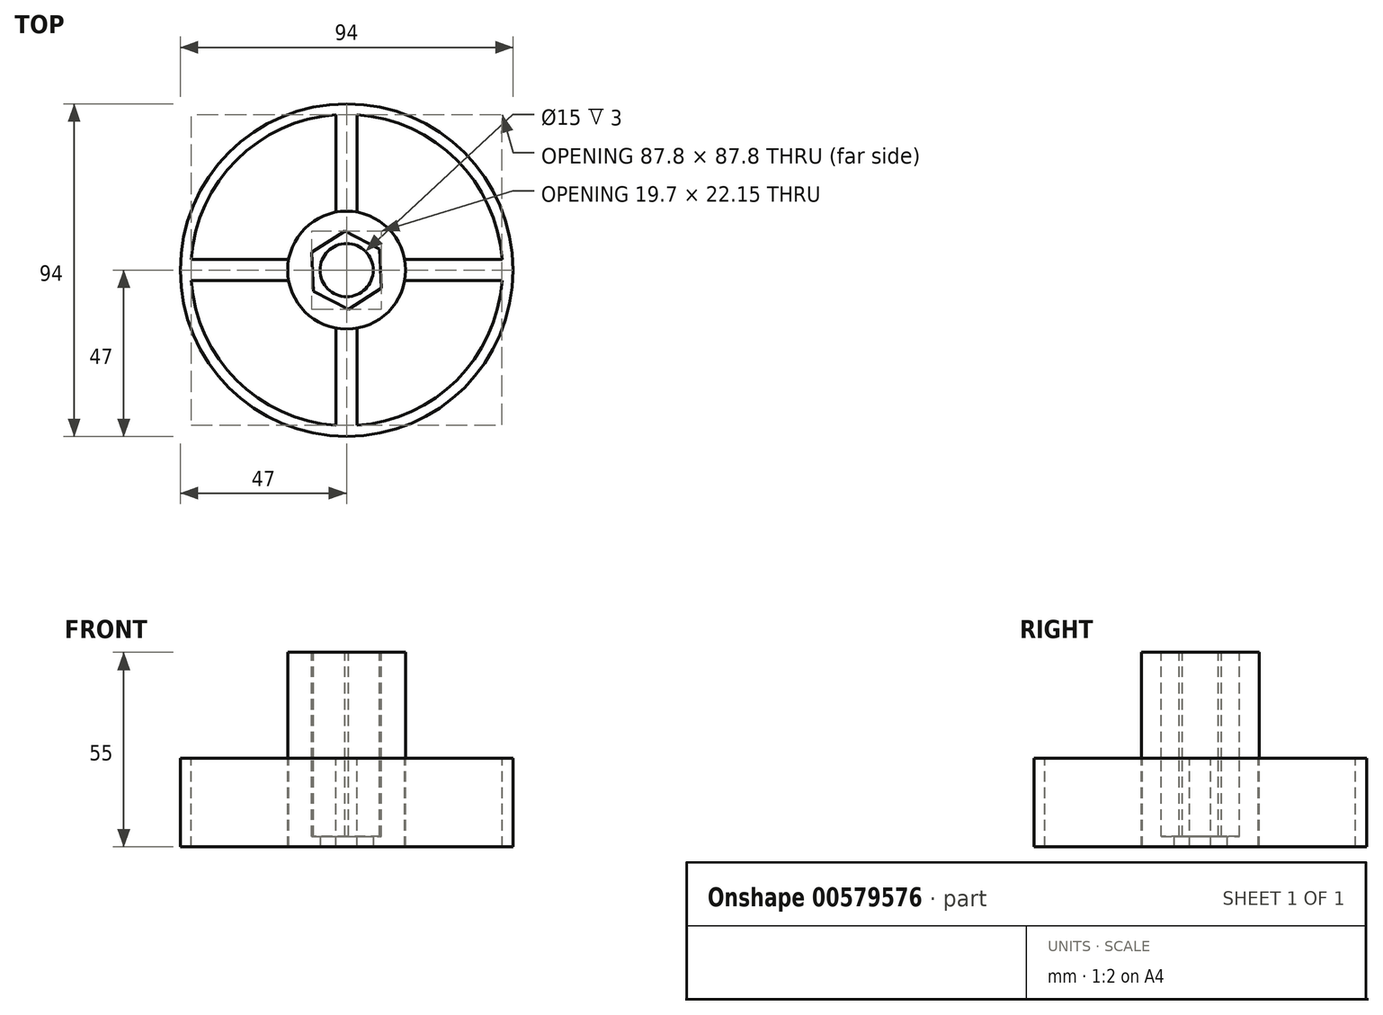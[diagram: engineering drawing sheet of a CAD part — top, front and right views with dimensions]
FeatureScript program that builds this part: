
annotation { "Feature Type Name" : "Feature", "Feature Type Description" : "" }
export const myFeature = defineFeature(function(context is Context, id is Id, definition is map)
    precondition{}
    {
        {
            var Q0;
            Q0=qCreatedBy(makeId("Top.planeOp"),FACE);
            var sketch = newSketch(context, id + "F0", { "sketchPlane" : qUnion([Q0])});
            skCircle(sketch, "E0.cCircle", {"center": v(0, 0) * mm, "radius": 9.6 * mm, "construction": true});
            skLineSegment(sketch, "E0.0", {"start": v(-9.85, 5.08) * mm, "end": v(-0.52, 11.07) * mm});
            skLineSegment(sketch, "E0.1", {"start": v(-0.52, 11.07) * mm, "end": v(9.33, 6) * mm});
            skLineSegment(sketch, "E0.2", {"start": v(9.33, 6) * mm, "end": v(9.85, -5.08) * mm});
            skLineSegment(sketch, "E0.3", {"start": v(9.85, -5.08) * mm, "end": v(0.52, -11.07) * mm});
            skLineSegment(sketch, "E0.4", {"start": v(0.52, -11.07) * mm, "end": v(-9.33, -6) * mm});
            skLineSegment(sketch, "E0.5", {"start": v(-9.33, -6) * mm, "end": v(-9.85, 5.08) * mm});
            skPoint(sketch, "E0.0.midPoint", {"position": v(-5.19, 8.08) * mm});
            skSolve(sketch);
        }
        {
            var Q0;
            Q0=qCreatedBy(makeId("Top.planeOp"),FACE);
            var sketch = newSketch(context, id + "F1", { "sketchPlane" : qUnion([Q0])});
            skCircle(sketch, "E1", {"center": v(0, 0) * mm, "radius": 16.65 * mm});
            skSolve(sketch);
        }
        {
            var Q0;
            Q0=makeQuery(id+"F1.imprint","IMPRINT",FACE,{"disambiguationData":[TD([[makeQuery(id+"F1.imprint","IMPRINT",EDGE,{"derivedFrom":sQuery(id+"F1.wireOp",EDGE,"E1")}),1.0]])]});
            extrude(context, id + "F2", {"entities" : qUnion([Q0]), "oppositeDirection" : true, "depth" : 30 * mm, "offsetDistance" : 25 * mm});
        }
        {
            var Q0;
            Q0=makeQuery(id+"F0.imprint","IMPRINT",FACE,{"disambiguationData":[TD([[makeQuery(id+"F0.imprint","IMPRINT",EDGE,{"derivedFrom":sQuery(id+"F0.wireOp",EDGE,"E0.0")}),-1.0]])]});
            extrude(context, id + "F3", {"entities" : qUnion([Q0]), "operationType" : NewBodyOperationType.REMOVE, "oppositeDirection" : true, "depth" : 31 * mm, "offsetDistance" : 25 * mm});
        }
        {
            var Q0;
            Q0=makeQuery(id+"F2.opExtrude","CAP_FACE",FACE,{"disambiguationData":[OSD([sQuery(id+"F1.wireOp",EDGE,"E1")])],"isStart":false});
            var sketch = newSketch(context, id + "F4", { "sketchPlane" : qUnion([Q0])});
            skCircle(sketch, "E2", {"center": v(0, 0) * mm, "radius": 7.5 * mm});
            skSolve(sketch);
        }
        {
            var Q0;
            Q0=makeQuery(id+"F4.imprint","IMPRINT",FACE,{"disambiguationData":[TD([[makeQuery(id+"F4.imprint","IMPRINT",EDGE,{"derivedFrom":sQuery(id+"F4.wireOp",EDGE,"E2")}),1.0]])]});
            extrude(context, id + "F5", {"entities" : qUnion([Q0]), "operationType" : NewBodyOperationType.REMOVE, "oppositeDirection" : true, "depth" : 25 * mm});
        }
        {
            var Q0;
            Q0=makeQuery(id+"F2.opExtrude","CAP_FACE",FACE,{"disambiguationData":[OSD([sQuery(id+"F1.wireOp",EDGE,"E1")])],"isStart":false});
            var sketch = newSketch(context, id + "F6", { "sketchPlane" : qUnion([Q0])});
            skCircle(sketch, "E3", {"center": v(0, 0) * mm, "radius": 47 * mm});
            skCircle(sketch, "E4", {"center": v(0, 0) * mm, "radius": 44 * mm});
            skPoint(sketch, "E5", {"position": v(-3, 0) * mm});
            skPoint(sketch, "E6", {"position": v(3, 0) * mm});
            skPoint(sketch, "E7", {"position": v(0, 3) * mm});
            skPoint(sketch, "E8", {"position": v(0, -3) * mm});
            skLineSegment(sketch, "E9", {"start": v(-3, 0) * mm, "end": v(-3, 43.9) * mm});
            skLineSegment(sketch, "E10", {"start": v(3, 0) * mm, "end": v(3, 43.9) * mm});
            skLineSegment(sketch, "E11", {"start": v(-3, 0) * mm, "end": v(-3, -43.9) * mm});
            skLineSegment(sketch, "E12", {"start": v(3, 0) * mm, "end": v(3, -43.9) * mm});
            skLineSegment(sketch, "E13", {"start": v(0, 3) * mm, "end": v(43.9, 3) * mm});
            skLineSegment(sketch, "E14", {"start": v(0, -3) * mm, "end": v(43.9, -3) * mm});
            skLineSegment(sketch, "E15", {"start": v(0, 3) * mm, "end": v(-43.9, 3) * mm});
            skLineSegment(sketch, "E16", {"start": v(0, -3) * mm, "end": v(-43.9, -3) * mm});
            skSolve(sketch);
        }
        {
            var Q0;
            Q0=makeQuery(id+"F6.imprint","IMPRINT",FACE,{"disambiguationData":[TD([[makeQuery(id+"F6.imprint","IMPRINT",EDGE,{"derivedFrom":sQuery(id+"F6.wireOp",EDGE,"E3")}),1.0]])]});
            var Q1;
            {var subQ0=sQuery(id+"F6.wireOp",EDGE,"E11");var subQ1=sQuery(id+"F6.wireOp",EDGE,"E4");var subQ2=makeQuery(id+"F6.imprint","INTERSECT",VERTEX,{"derivedFrom":[subQ1,subQ0]});Q1=makeQuery(id+"F6.imprint","IMPRINT",FACE,{"disambiguationData":[TD([[makeQuery(id+"F6.imprint","IMPRINT",EDGE,{"disambiguationData":[TD([[subQ2,-1.0]])],"derivedFrom":subQ1}),1.0]])]});}
            var Q2;
            {var subQ0=sQuery(id+"F6.wireOp",EDGE,"E13");var subQ1=sQuery(id+"F6.wireOp",EDGE,"E4");var subQ2=makeQuery(id+"F6.imprint","INTERSECT",VERTEX,{"derivedFrom":[subQ1,subQ0]});Q2=makeQuery(id+"F6.imprint","IMPRINT",FACE,{"disambiguationData":[TD([[makeQuery(id+"F6.imprint","IMPRINT",EDGE,{"disambiguationData":[TD([[subQ2,1.0]])],"derivedFrom":subQ1}),1.0]])]});}
            var Q3;
            {var subQ0=sQuery(id+"F6.wireOp",EDGE,"E15");var subQ1=sQuery(id+"F6.wireOp",EDGE,"E4");var subQ2=makeQuery(id+"F6.imprint","INTERSECT",VERTEX,{"derivedFrom":[subQ1,subQ0]});Q3=makeQuery(id+"F6.imprint","IMPRINT",FACE,{"disambiguationData":[TD([[makeQuery(id+"F6.imprint","IMPRINT",EDGE,{"disambiguationData":[TD([[subQ2,-1.0]])],"derivedFrom":subQ1}),1.0]])]});}
            var Q4;
            {var subQ0=sQuery(id+"F6.wireOp",EDGE,"E9");var subQ1=sQuery(id+"F6.wireOp",EDGE,"E4");var subQ2=makeQuery(id+"F6.imprint","INTERSECT",VERTEX,{"derivedFrom":[subQ1,subQ0]});Q4=makeQuery(id+"F6.imprint","IMPRINT",FACE,{"disambiguationData":[TD([[makeQuery(id+"F6.imprint","IMPRINT",EDGE,{"disambiguationData":[TD([[subQ2,1.0]])],"derivedFrom":subQ1}),1.0]])]});}
            extrude(context, id + "F7", {"entities" : qUnion([Q0, Q1, Q2, Q3, Q4]), "operationType" : NewBodyOperationType.ADD, "depth" : 25 * mm, "offsetDistance" : 25 * mm});
        }
        {
            var Q0;
            Q0=makeQuery(id+"F2.opExtrude","CAP_FACE",FACE,{"disambiguationData":[OSD([sQuery(id+"F1.wireOp",EDGE,"E1")])],"isStart":false});
            extrude(context, id + "F8", {"entities" : qUnion([Q0]), "depth" : 25 * mm, "offsetDistance" : 25 * mm});
        }
        {
            var Q0;
            Q0=makeQuery(id+"F8.opExtrude","CAP_FACE",FACE,{"disambiguationData":[OSD([sQuery(id+"F1.wireOp",EDGE,"E1")])],"isStart":false});
            var sketch = newSketch(context, id + "F9", { "sketchPlane" : qUnion([Q0])});
            skCircle(sketch, "E17", {"center": v(0, 0) * mm, "radius": 14.05 * mm});
            skCircle(sketch, "E18", {"center": v(0, 0) * mm, "radius": 7.5 * mm});
            skSolve(sketch);
        }
        {
            var Q0;
            Q0=makeQuery(id+"F9.imprint","IMPRINT",FACE,{"disambiguationData":[TD([[makeQuery(id+"F9.imprint","IMPRINT",EDGE,{"derivedFrom":sQuery(id+"F9.wireOp",EDGE,"E17")}),1.0]])]});
            var Q1;
            Q1=makeQuery(id+"F9.imprint","IMPRINT",FACE,{"disambiguationData":[TD([[makeQuery(id+"F9.imprint","IMPRINT",EDGE,{"derivedFrom":sQuery(id+"F9.wireOp",EDGE,"E18")}),-1.0]])]});
            extrude(context, id + "F10", {"entities" : qUnion([Q0, Q1]), "operationType" : NewBodyOperationType.ADD, "oppositeDirection" : true, "depth" : 3 * mm, "offsetDistance" : 25 * mm});
        }
    });
